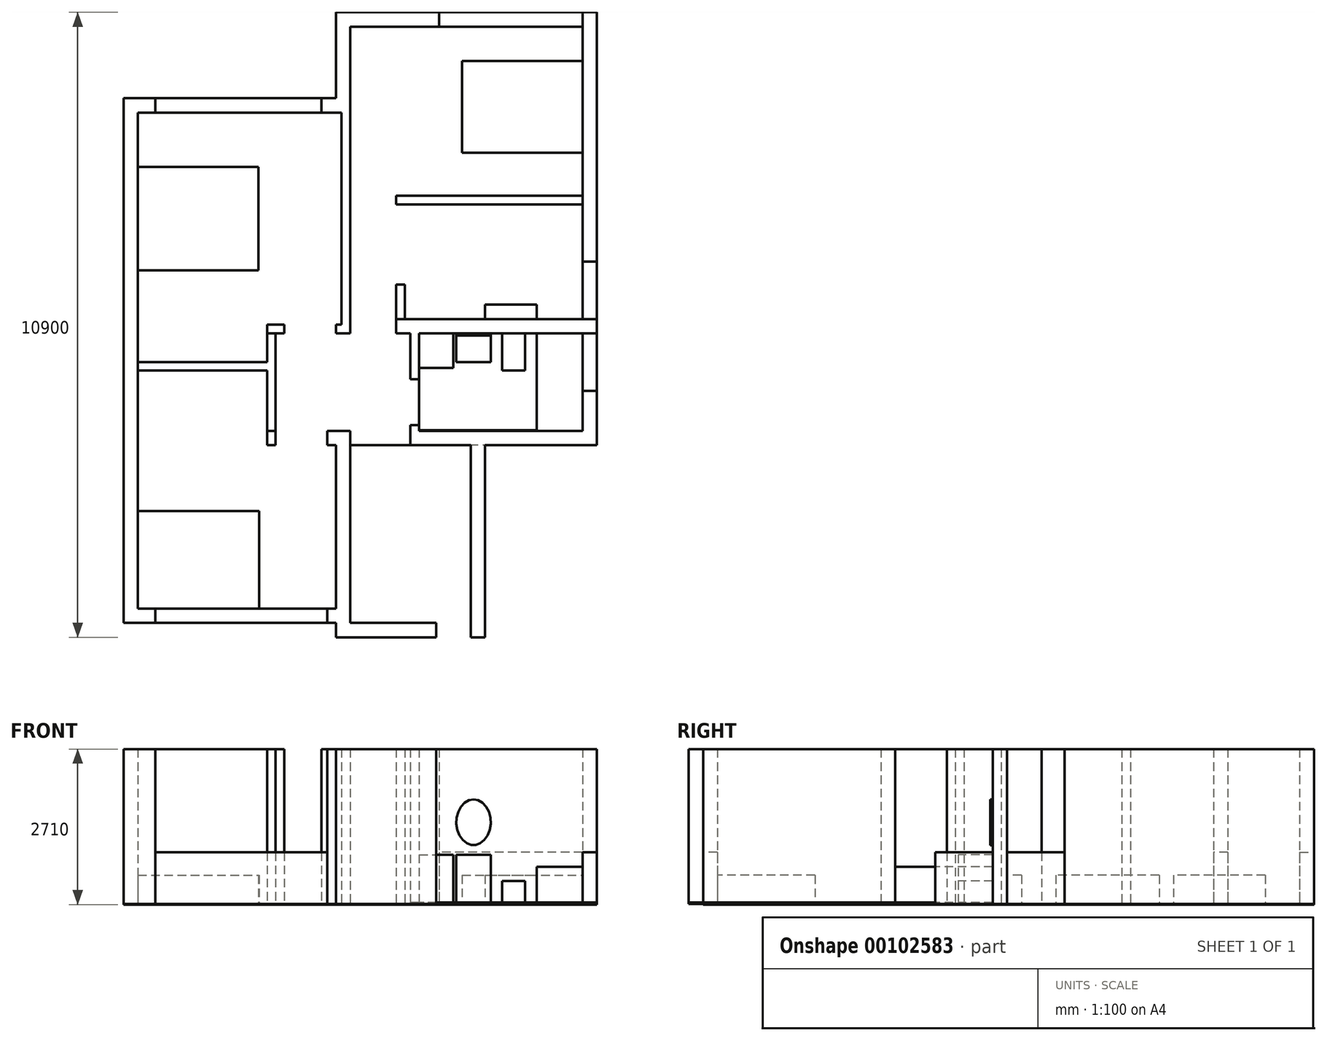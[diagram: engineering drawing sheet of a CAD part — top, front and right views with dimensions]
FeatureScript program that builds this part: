
annotation { "Feature Type Name" : "Feature", "Feature Type Description" : "" }
export const myFeature = defineFeature(function(context is Context, id is Id, definition is map)
    precondition{}
    {
        {
            var Q0;
            Q0=qCreatedBy(makeId("Top.planeOp"),FACE);
            var sketch = newSketch(context, id + "F0", { "sketchPlane" : qUnion([Q0])});
            skLineSegment(sketch, "E0.left", {"start": v(0, -3350) * mm, "end": v(0, 5800) * mm});
            skLineSegment(sketch, "E0.right", {"start": v(250, -250) * mm, "end": v(250, 5550) * mm});
            skLineSegment(sketch, "E1.bottom", {"start": v(0, 5800) * mm, "end": v(550, 5800) * mm});
            skLineSegment(sketch, "E1.top", {"start": v(250, 5550) * mm, "end": v(550, 5550) * mm});
            skLineSegment(sketch, "E1.right", {"start": v(550, 5800) * mm, "end": v(550, 5550) * mm});
            skLineSegment(sketch, "E2.top", {"start": v(0, -3350) * mm, "end": v(550, -3350) * mm});
            skLineSegment(sketch, "E2.right", {"start": v(250, -250) * mm, "end": v(250, -3100) * mm});
            skLineSegment(sketch, "E3.top", {"start": v(250, -3100) * mm, "end": v(550, -3100) * mm});
            skLineSegment(sketch, "E3.right", {"start": v(550, -3350) * mm, "end": v(550, -3100) * mm});
            skPoint(sketch, "E4.orphan", {"position": v(250, -3350) * mm});
            skLineSegment(sketch, "E5.bottom", {"start": v(3550, 0) * mm, "end": v(3950, 0) * mm});
            skLineSegment(sketch, "E5.top", {"start": v(3550, -250) * mm, "end": v(3700, -250) * mm});
            skLineSegment(sketch, "E5.left", {"start": v(3550, 0) * mm, "end": v(3550, -250) * mm});
            skLineSegment(sketch, "E5.right", {"start": v(3950, 0) * mm, "end": v(3950, -250) * mm});
            skLineSegment(sketch, "E6.bottom", {"start": v(3700, -3100) * mm, "end": v(3550, -3100) * mm});
            skLineSegment(sketch, "E6.top", {"start": v(3950, -3350) * mm, "end": v(3550, -3350) * mm});
            skLineSegment(sketch, "E6.left", {"start": v(3950, -3100) * mm, "end": v(3950, -3350) * mm});
            skLineSegment(sketch, "E6.right", {"start": v(3550, -3100) * mm, "end": v(3550, -3350) * mm});
            skLineSegment(sketch, "E7.left", {"start": v(3700, -250) * mm, "end": v(3700, -3100) * mm});
            skLineSegment(sketch, "E7.right", {"start": v(3950, -250) * mm, "end": v(3950, -3100) * mm});
            skLineSegment(sketch, "E8.bottom", {"start": v(3700, -3350) * mm, "end": v(5450, -3350) * mm});
            skLineSegment(sketch, "E8.top", {"start": v(3700, -3600) * mm, "end": v(5450, -3600) * mm});
            skLineSegment(sketch, "E8.left", {"start": v(3700, -3350) * mm, "end": v(3700, -3600) * mm});
            skLineSegment(sketch, "E8.right", {"start": v(5450, -3350) * mm, "end": v(5450, -3600) * mm});
            skLineSegment(sketch, "E9.top", {"start": v(6050, -3600) * mm, "end": v(6300, -3600) * mm});
            skLineSegment(sketch, "E9.left", {"start": v(6050, -250) * mm, "end": v(6050, -3600) * mm});
            skLineSegment(sketch, "E9.right", {"start": v(6300, -250) * mm, "end": v(6300, -3600) * mm});
            skLineSegment(sketch, "E10.bottom", {"start": v(5000, 0) * mm, "end": v(8125, 0) * mm});
            skLineSegment(sketch, "E10.top", {"start": v(5000, -250) * mm, "end": v(8125, -250) * mm});
            skLineSegment(sketch, "E10.left", {"start": v(5000, 0) * mm, "end": v(5000, -250) * mm});
            skPoint(sketch, "E11.endSnap0", {"position": v(3700, -1675) * mm});
            skLineSegment(sketch, "E12", {"start": v(3825, -963.9) * mm, "end": v(3825, 6299.29) * mm, "construction": true});
            skLineSegment(sketch, "E13", {"start": v(3550, -125) * mm, "end": v(6508.51, -125) * mm, "construction": true});
            skPoint(sketch, "E13.endSnap0", {"position": v(5250, -125) * mm});
            skLineSegment(sketch, "E14", {"start": v(8125, 470.93) * mm, "end": v(8125, -4199.5) * mm, "construction": true});
            skLineSegment(sketch, "E15", {"start": v(6175, -3600) * mm, "end": v(6175, 565.67) * mm, "construction": true});
            skPoint(sketch, "E15.endSnap0", {"position": v(6175, -3350) * mm});
            skPoint(sketch, "E16.orphan", {"position": v(5250, -250) * mm});
            skLineSegment(sketch, "E17", {"start": v(8125, 0) * mm, "end": v(8125, -250) * mm});
            skPoint(sketch, "E18.orphan", {"position": v(6050, -3350) * mm});
            skLineSegment(sketch, "E19.bottom", {"start": v(5000, 0) * mm, "end": v(5150, 0) * mm});
            skLineSegment(sketch, "E19.top", {"start": v(5000, 100) * mm, "end": v(5150, 100) * mm});
            skLineSegment(sketch, "E19.left", {"start": v(5000, 0) * mm, "end": v(5000, 100) * mm});
            skLineSegment(sketch, "E19.right", {"start": v(5150, 0) * mm, "end": v(5150, 100) * mm});
            skLineSegment(sketch, "E20.bottom", {"start": v(8125, 0) * mm, "end": v(8250, 0) * mm});
            skLineSegment(sketch, "E20.top", {"start": v(8125, -250) * mm, "end": v(8250, -250) * mm});
            skLineSegment(sketch, "E20.right", {"start": v(8250, 0) * mm, "end": v(8250, -250) * mm});
            skLineSegment(sketch, "E21.bottom", {"start": v(8250, 0) * mm, "end": v(8000, 0) * mm});
            skLineSegment(sketch, "E21.top", {"start": v(8250, 700) * mm, "end": v(8000, 700) * mm});
            skLineSegment(sketch, "E21.left", {"start": v(8250, 0) * mm, "end": v(8250, 700) * mm});
            skLineSegment(sketch, "E21.right", {"start": v(8000, 0) * mm, "end": v(8000, 700) * mm});
            skLineSegment(sketch, "E22.bottom", {"start": v(8250, 1700) * mm, "end": v(4750, 1700) * mm});
            skLineSegment(sketch, "E22.top", {"start": v(8250, 1950) * mm, "end": v(4750, 1950) * mm});
            skLineSegment(sketch, "E22.left", {"start": v(8250, 1700) * mm, "end": v(8250, 1950) * mm});
            skLineSegment(sketch, "E22.right", {"start": v(4750, 1700) * mm, "end": v(4750, 1950) * mm});
            skLineSegment(sketch, "E23.bottom", {"start": v(5000, 1700) * mm, "end": v(5150, 1700) * mm});
            skLineSegment(sketch, "E23.top", {"start": v(5000, 900) * mm, "end": v(5150, 900) * mm});
            skLineSegment(sketch, "E23.left", {"start": v(5000, 1700) * mm, "end": v(5000, 900) * mm});
            skLineSegment(sketch, "E23.right", {"start": v(5150, 1700) * mm, "end": v(5150, 900) * mm});
            skLineSegment(sketch, "E24.bottom", {"start": v(8250, 2950) * mm, "end": v(8000, 2950) * mm});
            skLineSegment(sketch, "E24.top", {"start": v(8250, 7300) * mm, "end": v(8000, 7300) * mm});
            skLineSegment(sketch, "E24.left", {"start": v(8250, 2950) * mm, "end": v(8250, 7300) * mm});
            skLineSegment(sketch, "E24.right", {"start": v(8000, 2950) * mm, "end": v(8000, 7300) * mm});
            skLineSegment(sketch, "E25", {"start": v(8250, 1825) * mm, "end": v(6731.2, 1825) * mm, "construction": true});
            skLineSegment(sketch, "E26", {"start": v(288.62, 5675) * mm, "end": v(10080.8, 5675) * mm, "construction": true});
            skPoint(sketch, "E27.firstSnap0", {"position": v(8125, 7300) * mm});
            skLineSegment(sketch, "E27.bottom", {"start": v(5500, 7300) * mm, "end": v(3950, 7300) * mm});
            skLineSegment(sketch, "E27.top", {"start": v(5500, 7050) * mm, "end": v(3950, 7050) * mm});
            skLineSegment(sketch, "E27.left", {"start": v(5500, 7300) * mm, "end": v(5500, 7050) * mm});
            skLineSegment(sketch, "E27.right", {"start": v(3950, 7300) * mm, "end": v(3950, 7050) * mm});
            skLineSegment(sketch, "E28.bottom", {"start": v(3950, 7300) * mm, "end": v(3700, 7300) * mm});
            skLineSegment(sketch, "E28.top", {"start": v(3950, 5550) * mm, "end": v(3700, 5550) * mm});
            skLineSegment(sketch, "E28.left", {"start": v(3950, 7300) * mm, "end": v(3950, 5550) * mm});
            skLineSegment(sketch, "E28.right", {"start": v(3700, 7300) * mm, "end": v(3700, 5550) * mm});
            skLineSegment(sketch, "E29.bottom", {"start": v(3700, 5550) * mm, "end": v(3450, 5550) * mm});
            skLineSegment(sketch, "E29.top", {"start": v(3700, 5800) * mm, "end": v(3450, 5800) * mm});
            skLineSegment(sketch, "E29.left", {"start": v(3700, 5550) * mm, "end": v(3700, 5800) * mm});
            skLineSegment(sketch, "E29.right", {"start": v(3450, 5550) * mm, "end": v(3450, 5800) * mm});
            skLineSegment(sketch, "E30.bottom", {"start": v(3800, 5550) * mm, "end": v(3950, 5550) * mm});
            skLineSegment(sketch, "E30.top", {"start": v(3800, 1700) * mm, "end": v(3950, 1700) * mm});
            skLineSegment(sketch, "E30.left", {"start": v(3800, 5550) * mm, "end": v(3800, 1700) * mm});
            skLineSegment(sketch, "E30.right", {"start": v(3950, 5550) * mm, "end": v(3950, 1700) * mm});
            skLineSegment(sketch, "E31.bottom", {"start": v(3800, 1700) * mm, "end": v(3700, 1700) * mm});
            skLineSegment(sketch, "E31.top", {"start": v(3800, 1850) * mm, "end": v(3700, 1850) * mm});
            skLineSegment(sketch, "E31.left", {"start": v(3800, 1700) * mm, "end": v(3800, 1850) * mm});
            skLineSegment(sketch, "E31.right", {"start": v(3700, 1700) * mm, "end": v(3700, 1850) * mm});
            skLineSegment(sketch, "E32.bottom", {"start": v(2800, 1700) * mm, "end": v(2500, 1700) * mm});
            skLineSegment(sketch, "E32.top", {"start": v(2800, 1850) * mm, "end": v(2500, 1850) * mm});
            skLineSegment(sketch, "E32.left", {"start": v(2800, 1700) * mm, "end": v(2800, 1850) * mm});
            skLineSegment(sketch, "E32.right", {"start": v(2500, 1700) * mm, "end": v(2500, 1850) * mm});
            skLineSegment(sketch, "E33.bottom", {"start": v(2650, -250) * mm, "end": v(2500, -250) * mm});
            skLineSegment(sketch, "E33.top", {"start": v(2650, 0) * mm, "end": v(2500, 0) * mm});
            skLineSegment(sketch, "E33.left", {"start": v(2650, -250) * mm, "end": v(2650, 0) * mm});
            skLineSegment(sketch, "E33.right", {"start": v(2500, -250) * mm, "end": v(2500, 0) * mm});
            skSolve(sketch);
        }
        {
            var Q0;
            Q0=qSketchRegion(id+"F0",true);
            extrude(context, id + "F1", {"entities" : qUnion([Q0]), "depth" : 2700 * mm});
        }
        {
            var Q0;
            Q0=qCreatedBy(makeId("Top.planeOp"),FACE);
            var sketch = newSketch(context, id + "F2", { "sketchPlane" : qUnion([Q0])});
            skLineSegment(sketch, "E34.bottom", {"start": v(8000, 7050) * mm, "end": v(5500, 7050) * mm});
            skLineSegment(sketch, "E34.top", {"start": v(8000, 7300) * mm, "end": v(5500, 7300) * mm});
            skLineSegment(sketch, "E34.left", {"start": v(8000, 7050) * mm, "end": v(8000, 7300) * mm});
            skLineSegment(sketch, "E34.right", {"start": v(5500, 7050) * mm, "end": v(5500, 7300) * mm});
            skLineSegment(sketch, "E35.bottom", {"start": v(8000, 2950) * mm, "end": v(8250, 2950) * mm});
            skLineSegment(sketch, "E35.top", {"start": v(8000, 1950) * mm, "end": v(8250, 1950) * mm});
            skLineSegment(sketch, "E35.left", {"start": v(8000, 2950) * mm, "end": v(8000, 1950) * mm});
            skLineSegment(sketch, "E35.right", {"start": v(8250, 2950) * mm, "end": v(8250, 1950) * mm});
            skLineSegment(sketch, "E36.bottom", {"start": v(550, -3100) * mm, "end": v(3550, -3100) * mm});
            skLineSegment(sketch, "E36.top", {"start": v(550, -3350) * mm, "end": v(3550, -3350) * mm});
            skLineSegment(sketch, "E36.left", {"start": v(550, -3100) * mm, "end": v(550, -3350) * mm});
            skLineSegment(sketch, "E36.right", {"start": v(3550, -3100) * mm, "end": v(3550, -3350) * mm});
            skLineSegment(sketch, "E37.bottom", {"start": v(550, 5800) * mm, "end": v(3450, 5800) * mm});
            skLineSegment(sketch, "E37.top", {"start": v(550, 5550) * mm, "end": v(3450, 5550) * mm});
            skLineSegment(sketch, "E37.left", {"start": v(550, 5800) * mm, "end": v(550, 5550) * mm});
            skLineSegment(sketch, "E37.right", {"start": v(3450, 5800) * mm, "end": v(3450, 5550) * mm});
            skLineSegment(sketch, "E38.bottom", {"start": v(8000, 1700) * mm, "end": v(8250, 1700) * mm});
            skLineSegment(sketch, "E38.top", {"start": v(8000, 700) * mm, "end": v(8250, 700) * mm});
            skLineSegment(sketch, "E38.left", {"start": v(8000, 1700) * mm, "end": v(8000, 700) * mm});
            skLineSegment(sketch, "E38.right", {"start": v(8250, 1700) * mm, "end": v(8250, 700) * mm});
            skSolve(sketch);
        }
        {
            var Q0;
            Q0=makeQuery(id+"F2.imprint","IMPRINT",FACE,{"disambiguationData":[TD([[makeQuery(id+"F2.imprint","IMPRINT",EDGE,{"derivedFrom":sQuery(id+"F2.wireOp",EDGE,"E34.bottom")}),-1.0]])]});
            var Q1;
            Q1=makeQuery(id+"F2.imprint","IMPRINT",FACE,{"disambiguationData":[TD([[makeQuery(id+"F2.imprint","IMPRINT",EDGE,{"derivedFrom":sQuery(id+"F2.wireOp",EDGE,"E37.bottom")}),-1.0]])]});
            var Q2;
            Q2=makeQuery(id+"F2.imprint","IMPRINT",FACE,{"disambiguationData":[TD([[makeQuery(id+"F2.imprint","IMPRINT",EDGE,{"derivedFrom":sQuery(id+"F2.wireOp",EDGE,"E36.bottom")}),-1.0]])]});
            var Q3;
            Q3=makeQuery(id+"F2.imprint","IMPRINT",FACE,{"disambiguationData":[TD([[makeQuery(id+"F2.imprint","IMPRINT",EDGE,{"derivedFrom":sQuery(id+"F2.wireOp",EDGE,"E35.bottom")}),-1.0]])]});
            var Q4;
            Q4=makeQuery(id+"F2.imprint","IMPRINT",FACE,{"disambiguationData":[TD([[makeQuery(id+"F2.imprint","IMPRINT",EDGE,{"derivedFrom":sQuery(id+"F2.wireOp",EDGE,"E38.bottom")}),-1.0]])]});
            extrude(context, id + "F3", {"entities" : qUnion([Q0, Q1, Q2, Q3, Q4]), "depth" : 900 * mm});
        }
        {
            var Q0;
            Q0=qCreatedBy(makeId("Top.planeOp"),FACE);
            var sketch = newSketch(context, id + "F4", { "sketchPlane" : qUnion([Q0])});
            skLineSegment(sketch, "E39", {"start": v(0, -3241.89) * mm, "end": v(0, 5800) * mm});
            skLineSegment(sketch, "E40", {"start": v(0, 5800) * mm, "end": v(3700, 5800) * mm});
            skLineSegment(sketch, "E41", {"start": v(3700, 5800) * mm, "end": v(3700, 7300) * mm});
            skLineSegment(sketch, "E42", {"start": v(3700, 7300) * mm, "end": v(8250, 7300) * mm});
            skLineSegment(sketch, "E43", {"start": v(8250, 7300) * mm, "end": v(8250, -250) * mm});
            skLineSegment(sketch, "E44", {"start": v(8250, -250) * mm, "end": v(3950, -250) * mm});
            skLineSegment(sketch, "E45", {"start": v(3950, -250) * mm, "end": v(3950, -3350) * mm});
            skLineSegment(sketch, "E46", {"start": v(3950, -3350) * mm, "end": v(0, -3350) * mm});
            skLineSegment(sketch, "E47", {"start": v(0, -3350) * mm, "end": v(0, -3241.89) * mm});
            skSolve(sketch);
        }
        {
            var Q0;
            Q0=qSketchRegion(id+"F4",true);
            extrude(context, id + "F5", {"entities" : qUnion([Q0]), "oppositeDirection" : true, "depth" : 10 * mm});
        }
        {
            var Q0;
            Q0=makeQuery(id+"F5.opExtrude","CAP_FACE",FACE,{"disambiguationData":[OSD([sQuery(id+"F4.wireOp",EDGE,"E39"),sQuery(id+"F4.wireOp",EDGE,"E40"),sQuery(id+"F4.wireOp",EDGE,"E41"),sQuery(id+"F4.wireOp",EDGE,"E42"),sQuery(id+"F4.wireOp",EDGE,"E43"),sQuery(id+"F4.wireOp",EDGE,"E44"),sQuery(id+"F4.wireOp",EDGE,"E45"),sQuery(id+"F4.wireOp",EDGE,"E46"),sQuery(id+"F4.wireOp",EDGE,"E47")])],"isStart":true});
            var sketch = newSketch(context, id + "F6", { "sketchPlane" : qUnion([Q0])});
            skLineSegment(sketch, "E48.bottom", {"start": v(6300, 2200) * mm, "end": v(7200, 2200) * mm});
            skLineSegment(sketch, "E48.top", {"start": v(6300, 1950) * mm, "end": v(7200, 1950) * mm});
            skLineSegment(sketch, "E48.left", {"start": v(6300, 2200) * mm, "end": v(6300, 1950) * mm});
            skLineSegment(sketch, "E48.right", {"start": v(7200, 2200) * mm, "end": v(7200, 1950) * mm});
            skSolve(sketch);
        }
        {
            var Q0;
            Q0=makeQuery(id+"F6.imprint","IMPRINT",FACE,{"disambiguationData":[TD([[makeQuery(id+"F6.imprint","IMPRINT",EDGE,{"derivedFrom":sQuery(id+"F6.wireOp",EDGE,"E48.bottom")}),-1.0]])]});
            extrude(context, id + "F7", {"entities" : qUnion([Q0]), "depth" : 500 * mm});
        }
        {
            var Q0;
            Q0=makeQuery(id+"F5.opExtrude","CAP_FACE",FACE,{"disambiguationData":[OSD([sQuery(id+"F4.wireOp",EDGE,"E39"),sQuery(id+"F4.wireOp",EDGE,"E40"),sQuery(id+"F4.wireOp",EDGE,"E41"),sQuery(id+"F4.wireOp",EDGE,"E42"),sQuery(id+"F4.wireOp",EDGE,"E43"),sQuery(id+"F4.wireOp",EDGE,"E44"),sQuery(id+"F4.wireOp",EDGE,"E45"),sQuery(id+"F4.wireOp",EDGE,"E46"),sQuery(id+"F4.wireOp",EDGE,"E47")])],"isStart":true});
            var sketch = newSketch(context, id + "F8", { "sketchPlane" : qUnion([Q0])});
            skLineSegment(sketch, "E49.bottom", {"start": v(4750, 4100) * mm, "end": v(8000, 4100) * mm});
            skLineSegment(sketch, "E49.top", {"start": v(4750, 3950) * mm, "end": v(8000, 3950) * mm});
            skLineSegment(sketch, "E49.left", {"start": v(4750, 3950) * mm, "end": v(4750, 3450) * mm});
            skLineSegment(sketch, "E49.right", {"start": v(8000, 4100) * mm, "end": v(8000, 3950) * mm});
            skLineSegment(sketch, "E50.bottom", {"start": v(4750, 3950) * mm, "end": v(4900, 3950) * mm});
            skLineSegment(sketch, "E50.top", {"start": v(4750, 3350) * mm, "end": v(4900, 3350) * mm});
            skLineSegment(sketch, "E50.left", {"start": v(4750, 3450) * mm, "end": v(4750, 3350) * mm});
            skLineSegment(sketch, "E50.right", {"start": v(4900, 3950) * mm, "end": v(4900, 3350) * mm});
            skLineSegment(sketch, "E51.bottom", {"start": v(4750, 2550) * mm, "end": v(4900, 2550) * mm});
            skLineSegment(sketch, "E51.top", {"start": v(4750, 1950) * mm, "end": v(4900, 1950) * mm});
            skLineSegment(sketch, "E51.left", {"start": v(4750, 2550) * mm, "end": v(4750, 1950) * mm});
            skLineSegment(sketch, "E51.right", {"start": v(4900, 2550) * mm, "end": v(4900, 1950) * mm});
            skLineSegment(sketch, "E52", {"start": v(4750, 4100) * mm, "end": v(4750, 3950) * mm});
            skSolve(sketch);
        }
        {
            var Q0;
            Q0=makeQuery(id+"F8.imprint","IMPRINT",FACE,{"disambiguationData":[TD([[makeQuery(id+"F8.imprint","IMPRINT",EDGE,{"derivedFrom":sQuery(id+"F8.wireOp",EDGE,"E49.bottom")}),-1.0]])]});
            var Q1;
            Q1=makeQuery(id+"F8.imprint","IMPRINT",FACE,{"disambiguationData":[TD([[makeQuery(id+"F8.imprint","IMPRINT",EDGE,{"derivedFrom":sQuery(id+"F8.wireOp",EDGE,"E50.bottom")}),-1.0]])]});
            var Q2;
            Q2=makeQuery(id+"F8.imprint","IMPRINT",FACE,{"disambiguationData":[TD([[makeQuery(id+"F8.imprint","IMPRINT",EDGE,{"derivedFrom":sQuery(id+"F8.wireOp",EDGE,"E51.bottom")}),-1.0]])]});
            extrude(context, id + "F9", {"entities" : qUnion([Q0, Q1, Q2]), "depth" : 2700 * mm});
        }
        {
            var Q0;
            Q0=makeQuery(id+"F5.opExtrude","CAP_FACE",FACE,{"disambiguationData":[OSD([sQuery(id+"F4.wireOp",EDGE,"E39"),sQuery(id+"F4.wireOp",EDGE,"E40"),sQuery(id+"F4.wireOp",EDGE,"E41"),sQuery(id+"F4.wireOp",EDGE,"E42"),sQuery(id+"F4.wireOp",EDGE,"E43"),sQuery(id+"F4.wireOp",EDGE,"E44"),sQuery(id+"F4.wireOp",EDGE,"E45"),sQuery(id+"F4.wireOp",EDGE,"E46"),sQuery(id+"F4.wireOp",EDGE,"E47")])],"isStart":true});
            var sketch = newSketch(context, id + "F10", { "sketchPlane" : qUnion([Q0])});
            skLineSegment(sketch, "E53.bottom", {"start": v(2500, 0) * mm, "end": v(2650, 0) * mm});
            skLineSegment(sketch, "E53.top", {"start": v(2500, 1700) * mm, "end": v(2650, 1700) * mm});
            skLineSegment(sketch, "E53.left", {"start": v(2500, 0) * mm, "end": v(2500, 1700) * mm});
            skLineSegment(sketch, "E53.right", {"start": v(2650, 0) * mm, "end": v(2650, 1700) * mm});
            skLineSegment(sketch, "E54.bottom", {"start": v(250, 1200) * mm, "end": v(2500, 1200) * mm});
            skLineSegment(sketch, "E54.top", {"start": v(250, 1050) * mm, "end": v(2500, 1050) * mm});
            skLineSegment(sketch, "E54.left", {"start": v(250, 1200) * mm, "end": v(250, 1050) * mm});
            skLineSegment(sketch, "E54.right", {"start": v(2500, 1200) * mm, "end": v(2500, 1050) * mm});
            skSolve(sketch);
        }
        {
            var Q0;
            Q0 = qSketchRegion(id + "F10", true);
            extrude(context, id + "F11", {"entities" : qUnion([Q0]), "depth" : 2700 * mm});
        }
        {
            var Q0;
            Q0=makeQuery(id+"F5.opExtrude","CAP_FACE",FACE,{"disambiguationData":[OSD([sQuery(id+"F4.wireOp",EDGE,"E39"),sQuery(id+"F4.wireOp",EDGE,"E40"),sQuery(id+"F4.wireOp",EDGE,"E41"),sQuery(id+"F4.wireOp",EDGE,"E42"),sQuery(id+"F4.wireOp",EDGE,"E43"),sQuery(id+"F4.wireOp",EDGE,"E44"),sQuery(id+"F4.wireOp",EDGE,"E45"),sQuery(id+"F4.wireOp",EDGE,"E46"),sQuery(id+"F4.wireOp",EDGE,"E47")])],"isStart":true});
            var sketch = newSketch(context, id + "F12", { "sketchPlane" : qUnion([Q0])});
            skLineSegment(sketch, "E55.bottom", {"start": v(250, -250) * mm, "end": v(2500, -250) * mm});
            skLineSegment(sketch, "E55.top", {"start": v(250, -100) * mm, "end": v(2500, -100) * mm});
            skLineSegment(sketch, "E55.left", {"start": v(250, -250) * mm, "end": v(250, -100) * mm});
            skLineSegment(sketch, "E55.right", {"start": v(2500, -250) * mm, "end": v(2500, -100) * mm});
            skLineSegment(sketch, "E56.bottom", {"start": v(250, 1850) * mm, "end": v(2500, 1850) * mm});
            skLineSegment(sketch, "E56.top", {"start": v(250, 1700) * mm, "end": v(2500, 1700) * mm});
            skLineSegment(sketch, "E56.left", {"start": v(250, 1850) * mm, "end": v(250, 1700) * mm});
            skLineSegment(sketch, "E56.right", {"start": v(2500, 1850) * mm, "end": v(2500, 1700) * mm});
            skLineSegment(sketch, "E57.bottom", {"start": v(2500, 925.22) * mm, "end": v(2540, 925.22) * mm});
            skLineSegment(sketch, "E57.top", {"start": v(2500, 0) * mm, "end": v(2540, 0) * mm});
            skLineSegment(sketch, "E57.left", {"start": v(2500, 925.22) * mm, "end": v(2500, 0) * mm});
            skLineSegment(sketch, "E57.right", {"start": v(2540, 925.22) * mm, "end": v(2540, 0) * mm});
            skLineSegment(sketch, "E58.bottom", {"start": v(2540, 925.22) * mm, "end": v(2580, 925.22) * mm});
            skLineSegment(sketch, "E58.top", {"start": v(2540, 1700) * mm, "end": v(2580, 1700) * mm});
            skLineSegment(sketch, "E58.left", {"start": v(2540, 925.22) * mm, "end": v(2540, 1700) * mm});
            skLineSegment(sketch, "E58.right", {"start": v(2580, 925.22) * mm, "end": v(2580, 1700) * mm});
            skSolve(sketch);
        }
        {
            var Q0;
            Q0=makeQuery(id+"F5.opExtrude","CAP_FACE",FACE,{"disambiguationData":[OSD([sQuery(id+"F4.wireOp",EDGE,"E39"),sQuery(id+"F4.wireOp",EDGE,"E40"),sQuery(id+"F4.wireOp",EDGE,"E41"),sQuery(id+"F4.wireOp",EDGE,"E42"),sQuery(id+"F4.wireOp",EDGE,"E43"),sQuery(id+"F4.wireOp",EDGE,"E44"),sQuery(id+"F4.wireOp",EDGE,"E45"),sQuery(id+"F4.wireOp",EDGE,"E46"),sQuery(id+"F4.wireOp",EDGE,"E47")])],"isStart":true});
            var sketch = newSketch(context, id + "F13", { "sketchPlane" : qUnion([Q0])});
            skLineSegment(sketch, "E59.bottom", {"start": v(5900, 6450) * mm, "end": v(8000, 6450) * mm});
            skLineSegment(sketch, "E59.top", {"start": v(5900, 4850) * mm, "end": v(8000, 4850) * mm});
            skLineSegment(sketch, "E59.left", {"start": v(5900, 6450) * mm, "end": v(5900, 4850) * mm});
            skLineSegment(sketch, "E59.right", {"start": v(8000, 6450) * mm, "end": v(8000, 4850) * mm});
            skLineSegment(sketch, "E60.bottom", {"start": v(250, 4600) * mm, "end": v(2350, 4600) * mm});
            skLineSegment(sketch, "E60.top", {"start": v(250, 2800) * mm, "end": v(2350, 2800) * mm});
            skLineSegment(sketch, "E60.left", {"start": v(250, 4600) * mm, "end": v(250, 2800) * mm});
            skLineSegment(sketch, "E60.right", {"start": v(2350, 4600) * mm, "end": v(2350, 2800) * mm});
            skLineSegment(sketch, "E61.bottom", {"start": v(250, -1400) * mm, "end": v(2360, -1400) * mm});
            skLineSegment(sketch, "E61.top", {"start": v(250, -3100) * mm, "end": v(2360, -3100) * mm});
            skLineSegment(sketch, "E61.left", {"start": v(250, -1400) * mm, "end": v(250, -3100) * mm});
            skLineSegment(sketch, "E61.right", {"start": v(2360, -1400) * mm, "end": v(2360, -3100) * mm});
            skLineSegment(sketch, "E62", {"start": v(250, -2200) * mm, "end": v(2360, -2200) * mm});
            skSolve(sketch);
        }
        {
            var Q0;
            Q0 = qSketchRegion(id + "F13", true);
            extrude(context, id + "F14", {"entities" : qUnion([Q0]), "depth" : 500 * mm});
        }
        {
            var Q0;
            Q0=makeQuery(id+"F5.opExtrude","CAP_FACE",FACE,{"disambiguationData":[OSD([sQuery(id+"F4.wireOp",EDGE,"E39"),sQuery(id+"F4.wireOp",EDGE,"E40"),sQuery(id+"F4.wireOp",EDGE,"E41"),sQuery(id+"F4.wireOp",EDGE,"E42"),sQuery(id+"F4.wireOp",EDGE,"E43"),sQuery(id+"F4.wireOp",EDGE,"E44"),sQuery(id+"F4.wireOp",EDGE,"E45"),sQuery(id+"F4.wireOp",EDGE,"E46"),sQuery(id+"F4.wireOp",EDGE,"E47")])],"isStart":true});
            var sketch = newSketch(context, id + "F15", { "sketchPlane" : qUnion([Q0])});
            skLineSegment(sketch, "E63.bottom", {"start": v(7200, 1700) * mm, "end": v(8000, 1700) * mm});
            skLineSegment(sketch, "E63.top", {"start": v(7200, 0) * mm, "end": v(8000, 0) * mm});
            skLineSegment(sketch, "E63.left", {"start": v(7200, 1700) * mm, "end": v(7200, 0) * mm});
            skLineSegment(sketch, "E63.right", {"start": v(8000, 1700) * mm, "end": v(8000, 0) * mm});
            skSolve(sketch);
        }
        {
            var Q0;
            Q0=makeQuery(id+"F15.imprint","IMPRINT",FACE,{"disambiguationData":[TD([[makeQuery(id+"F15.imprint","IMPRINT",EDGE,{"derivedFrom":sQuery(id+"F15.wireOp",EDGE,"E63.bottom")}),-1.0]])]});
            extrude(context, id + "F16", {"entities" : qUnion([Q0]), "depth" : 650 * mm});
        }
        {
            var Q0;
            Q0=makeQuery(id+"F5.opExtrude","CAP_FACE",FACE,{"disambiguationData":[OSD([sQuery(id+"F4.wireOp",EDGE,"E39"),sQuery(id+"F4.wireOp",EDGE,"E40"),sQuery(id+"F4.wireOp",EDGE,"E41"),sQuery(id+"F4.wireOp",EDGE,"E42"),sQuery(id+"F4.wireOp",EDGE,"E43"),sQuery(id+"F4.wireOp",EDGE,"E44"),sQuery(id+"F4.wireOp",EDGE,"E45"),sQuery(id+"F4.wireOp",EDGE,"E46"),sQuery(id+"F4.wireOp",EDGE,"E47")])],"isStart":true});
            var sketch = newSketch(context, id + "F17", { "sketchPlane" : qUnion([Q0])});
            skLineSegment(sketch, "E64.bottom", {"start": v(5150, 1700) * mm, "end": v(5750, 1700) * mm});
            skLineSegment(sketch, "E64.top", {"start": v(5150, 1100) * mm, "end": v(5750, 1100) * mm});
            skLineSegment(sketch, "E64.left", {"start": v(5150, 1700) * mm, "end": v(5150, 1100) * mm});
            skLineSegment(sketch, "E64.right", {"start": v(5750, 1700) * mm, "end": v(5750, 1100) * mm});
            skSolve(sketch);
        }
        {
            var Q0;
            Q0 = qSketchRegion(id + "F17", true);
            extrude(context, id + "F18", {"entities" : qUnion([Q0]), "depth" : 860 * mm});
        }
        {
            var Q0;
            Q0=makeQuery(id+"F5.opExtrude","CAP_FACE",FACE,{"disambiguationData":[OSD([sQuery(id+"F4.wireOp",EDGE,"E39"),sQuery(id+"F4.wireOp",EDGE,"E40"),sQuery(id+"F4.wireOp",EDGE,"E41"),sQuery(id+"F4.wireOp",EDGE,"E42"),sQuery(id+"F4.wireOp",EDGE,"E43"),sQuery(id+"F4.wireOp",EDGE,"E44"),sQuery(id+"F4.wireOp",EDGE,"E45"),sQuery(id+"F4.wireOp",EDGE,"E46"),sQuery(id+"F4.wireOp",EDGE,"E47")])],"isStart":true});
            var sketch = newSketch(context, id + "F19", { "sketchPlane" : qUnion([Q0])});
            skLineSegment(sketch, "E65.bottom", {"start": v(5800, 1700) * mm, "end": v(6400, 1700) * mm});
            skLineSegment(sketch, "E65.top", {"start": v(5800, 1200) * mm, "end": v(6400, 1200) * mm});
            skLineSegment(sketch, "E65.left", {"start": v(5800, 1700) * mm, "end": v(5800, 1200) * mm});
            skLineSegment(sketch, "E65.right", {"start": v(6400, 1700) * mm, "end": v(6400, 1200) * mm});
            skLineSegment(sketch, "E66", {"start": v(6100, 1700) * mm, "end": v(6100, 1402.26) * mm, "construction": true});
            skSolve(sketch);
        }
        {
            var Q0;
            Q0 = qSketchRegion(id + "F19", true);
            extrude(context, id + "F20", {"entities" : qUnion([Q0]), "depth" : 860 * mm});
        }
        {
            var Q0;
            Q0=makeQuery(id+"F5.opExtrude","CAP_FACE",FACE,{"disambiguationData":[OSD([sQuery(id+"F4.wireOp",EDGE,"E39"),sQuery(id+"F4.wireOp",EDGE,"E40"),sQuery(id+"F4.wireOp",EDGE,"E41"),sQuery(id+"F4.wireOp",EDGE,"E42"),sQuery(id+"F4.wireOp",EDGE,"E43"),sQuery(id+"F4.wireOp",EDGE,"E44"),sQuery(id+"F4.wireOp",EDGE,"E45"),sQuery(id+"F4.wireOp",EDGE,"E46"),sQuery(id+"F4.wireOp",EDGE,"E47")])],"isStart":true});
            var sketch = newSketch(context, id + "F21", { "sketchPlane" : qUnion([Q0])});
            skLineSegment(sketch, "E67.bottom", {"start": v(6600, 1700) * mm, "end": v(7000, 1700) * mm});
            skLineSegment(sketch, "E67.top", {"start": v(6600, 1050) * mm, "end": v(7000, 1050) * mm});
            skLineSegment(sketch, "E67.left", {"start": v(6600, 1700) * mm, "end": v(6600, 1050) * mm});
            skLineSegment(sketch, "E67.right", {"start": v(7000, 1700) * mm, "end": v(7000, 1050) * mm});
            skLineSegment(sketch, "E68", {"start": v(6800, 1700) * mm, "end": v(6800, 1387.73) * mm, "construction": true});
            skSolve(sketch);
        }
        {
            var Q0;
            Q0 = qSketchRegion(id + "F21", true);
            extrude(context, id + "F22", {"entities" : qUnion([Q0]), "depth" : 400 * mm});
        }
        {
            var Q0;
            Q0=makeQuery(id+"F5.opExtrude","CAP_FACE",FACE,{"disambiguationData":[OSD([sQuery(id+"F4.wireOp",EDGE,"E39"),sQuery(id+"F4.wireOp",EDGE,"E40"),sQuery(id+"F4.wireOp",EDGE,"E41"),sQuery(id+"F4.wireOp",EDGE,"E42"),sQuery(id+"F4.wireOp",EDGE,"E43"),sQuery(id+"F4.wireOp",EDGE,"E44"),sQuery(id+"F4.wireOp",EDGE,"E45"),sQuery(id+"F4.wireOp",EDGE,"E46"),sQuery(id+"F4.wireOp",EDGE,"E47")])],"isStart":true});
            var sketch = newSketch(context, id + "F23", { "sketchPlane" : qUnion([Q0])});
            skLineSegment(sketch, "E69.bottom", {"start": v(5150, 1700) * mm, "end": v(8000, 1700) * mm});
            skLineSegment(sketch, "E69.top", {"start": v(5150, 10) * mm, "end": v(8000, 10) * mm});
            skLineSegment(sketch, "E69.left", {"start": v(5150, 1700) * mm, "end": v(5150, 10) * mm});
            skLineSegment(sketch, "E69.right", {"start": v(8000, 1700) * mm, "end": v(8000, 10) * mm});
            skSolve(sketch);
        }
        {
            var Q0;
            Q0=makeQuery(id+"F23.imprint","IMPRINT",FACE,{"disambiguationData":[TD([[makeQuery(id+"F23.imprint","IMPRINT",EDGE,{"derivedFrom":sQuery(id+"F23.wireOp",EDGE,"E69.bottom")}),-1.0]])]});
            extrude(context, id + "F24", {"entities" : qUnion([Q0]), "depth" : 25 * mm});
        }
        {
            var Q0;
            {var subQ0=sQuery(id+"F0.wireOp",EDGE,"E22.bottom");Q0=makeQuery(id+"F1.opExtrude","SWEPT_FACE",FACE,{"disambiguationData":[OSD([subQ0]),TDD([makeQuery(id+"F0.imprint","IMPRINT",EDGE,{"disambiguationData":[TD([[makeQuery(id+"F0.imprint","INTERSECT",VERTEX,{"derivedFrom":[subQ0,sQuery(id+"F0.wireOp",EDGE,"E22.left")]}),-1.0]])],"derivedFrom":subQ0})])]});}
            var sketch = newSketch(context, id + "F25", { "sketchPlane" : qUnion([Q0])});
            skLineSegment(sketch, "E70.bottom", {"start": v(5150, 2100) * mm, "end": v(8250, 2100) * mm});
            skLineSegment(sketch, "E70.top", {"start": v(5150, 0) * mm, "end": v(8250, 0) * mm});
            skLineSegment(sketch, "E70.left", {"start": v(5150, 2100) * mm, "end": v(5150, 0) * mm});
            skLineSegment(sketch, "E70.right", {"start": v(8250, 2100) * mm, "end": v(8250, 0) * mm});
            skSolve(sketch);
        }
        {
            var Q0;
            Q0=makeQuery(id+"F1.opExtrude","CAP_FACE",FACE,{"disambiguationData":[OSD([sQuery(id+"F0.wireOp",EDGE,"E9.top"),sQuery(id+"F0.wireOp",EDGE,"E9.left"),sQuery(id+"F0.wireOp",EDGE,"E9.right"),sQuery(id+"F0.wireOp",EDGE,"E10.bottom"),sQuery(id+"F0.wireOp",EDGE,"E10.top"),sQuery(id+"F0.wireOp",EDGE,"E10.left"),sQuery(id+"F0.wireOp",EDGE,"E19.top"),sQuery(id+"F0.wireOp",EDGE,"E19.left"),sQuery(id+"F0.wireOp",EDGE,"E19.right"),sQuery(id+"F0.wireOp",EDGE,"E20.top"),sQuery(id+"F0.wireOp",EDGE,"E20.right"),sQuery(id+"F0.wireOp",EDGE,"E21.top"),sQuery(id+"F0.wireOp",EDGE,"E21.left"),sQuery(id+"F0.wireOp",EDGE,"E21.right")])],"isStart":false});
            var Q1;
            Q1=makeQuery(id+"F24.opExtrude","CAP_FACE",FACE,{"disambiguationData":[OSD([sQuery(id+"F23.wireOp",EDGE,"E69.bottom"),sQuery(id+"F23.wireOp",EDGE,"E69.top"),sQuery(id+"F23.wireOp",EDGE,"E69.left"),sQuery(id+"F23.wireOp",EDGE,"E69.right")])],"isStart":false});
            extrude(context, id + "F26", {"entities" : qUnion([Q0]), "operationType" : NewBodyOperationType.REMOVE, "endBound" : BoundingType.UP_TO_SURFACE, "oppositeDirection" : true, "depth" : 25 * mm, "endBoundEntityFace" : qUnion([Q1]), "offsetDistance" : 25 * mm});
        }
        {
            var Q0;
            Q0=makeQuery(id+"F25.imprint","IMPRINT",FACE,{"disambiguationData":[TD([[makeQuery(id+"F25.imprint","IMPRINT",EDGE,{"derivedFrom":sQuery(id+"F25.wireOp",EDGE,"E70.bottom")}),-1.0]])]});
            var sketch = newSketch(context, id + "F27", { "sketchPlane" : qUnion([Q0])});
            skPoint(sketch, "E71.middle", {"position": v(6100, 1425) * mm});
            skEllipse(sketch, "E72", {"center": v(6100, 1425) * mm, "majorRadius": 400 * mm, "minorRadius": 300 * mm, "majorAxis": v(0, 1)});
            skFitSpline(sketch, "E73.0", {"points": [v(6106.8, 1804.92) * mm, v(6100, 1805.04) * mm, v(6093.2, 1804.92) * mm, v(6084.19, 1804.48) * mm, v(6072.96, 1803.36) * mm, v(6059.59, 1801.15) * mm, v(6041.91, 1797.03) * mm, v(6020.15, 1789.74) * mm, v(5994.72, 1777.6) * mm, v(5974.25, 1764.7) * mm, v(5958.4, 1752.75) * mm, v(5946.8, 1742.98) * mm, v(5935.5, 1732.4) * mm, v(5926.39, 1722.93) * mm, v(5919.27, 1714.97) * mm, v(5914.03, 1708.8) * mm, v(5909.75, 1703.5) * mm, v(5906.37, 1699.15) * mm, v(5903.86, 1695.85) * mm, v(5901.38, 1692.5) * mm, v(5898.13, 1688) * mm, v(5894.13, 1682.26) * mm, v(5889.48, 1675.23) * mm, v(5883.45, 1665.66) * mm, v(5876.26, 1653.36) * mm, v(5868.2, 1638.06) * mm, v(5860.7, 1622.26) * mm, v(5851.51, 1600.57) * mm, v(5841.52, 1572.38) * mm, v(5833.62, 1542.97) * mm, v(5828.6, 1518.84) * mm, v(5825.48, 1500.47) * mm, v(5823.05, 1481.87) * mm, v(5821.59, 1466.2) * mm, v(5820.77, 1453.6) * mm, v(5820.33, 1444.1) * mm, v(5820.1, 1436.15) * mm, v(5820.01, 1429.78) * mm, v(5820, 1425) * mm, v(5820.01, 1420.22) * mm, v(5820.1, 1413.85) * mm, v(5820.33, 1405.9) * mm, v(5820.77, 1396.4) * mm, v(5821.59, 1383.8) * mm, v(5823.05, 1368.13) * mm, v(5825.48, 1349.53) * mm, v(5828.6, 1331.16) * mm, v(5833.62, 1307.03) * mm, v(5841.52, 1277.62) * mm, v(5851.51, 1249.43) * mm, v(5860.7, 1227.74) * mm, v(5868.2, 1211.94) * mm, v(5876.26, 1196.64) * mm, v(5883.45, 1184.34) * mm, v(5889.48, 1174.77) * mm, v(5894.13, 1167.74) * mm, v(5898.13, 1162) * mm, v(5901.38, 1157.5) * mm, v(5903.86, 1154.15) * mm, v(5906.37, 1150.85) * mm, v(5909.75, 1146.5) * mm, v(5914.03, 1141.2) * mm, v(5919.27, 1135.03) * mm, v(5926.39, 1127.07) * mm, v(5935.5, 1117.6) * mm, v(5946.8, 1107.02) * mm, v(5958.4, 1097.25) * mm, v(5974.25, 1085.3) * mm, v(5994.72, 1072.4) * mm, v(6020.15, 1060.26) * mm, v(6041.91, 1052.97) * mm, v(6059.59, 1048.85) * mm, v(6072.96, 1046.64) * mm, v(6084.19, 1045.52) * mm, v(6093.2, 1045.08) * mm, v(6100, 1044.96) * mm, v(6106.8, 1045.08) * mm, v(6115.81, 1045.52) * mm, v(6127.04, 1046.64) * mm, v(6140.41, 1048.85) * mm, v(6158.09, 1052.97) * mm, v(6179.85, 1060.26) * mm, v(6205.28, 1072.4) * mm, v(6225.75, 1085.3) * mm, v(6241.6, 1097.25) * mm, v(6253.2, 1107.02) * mm, v(6264.5, 1117.6) * mm, v(6273.61, 1127.07) * mm, v(6280.73, 1135.03) * mm, v(6285.97, 1141.2) * mm, v(6290.25, 1146.5) * mm, v(6293.63, 1150.85) * mm, v(6296.14, 1154.15) * mm, v(6298.62, 1157.5) * mm, v(6301.87, 1162) * mm, v(6305.87, 1167.74) * mm, v(6310.52, 1174.77) * mm, v(6316.55, 1184.34) * mm, v(6323.74, 1196.64) * mm, v(6331.8, 1211.94) * mm, v(6339.3, 1227.74) * mm, v(6348.49, 1249.43) * mm, v(6358.48, 1277.62) * mm, v(6366.38, 1307.03) * mm, v(6371.4, 1331.16) * mm, v(6374.52, 1349.53) * mm, v(6376.95, 1368.13) * mm, v(6378.41, 1383.8) * mm, v(6379.23, 1396.4) * mm, v(6379.67, 1405.9) * mm, v(6379.9, 1413.85) * mm, v(6379.99, 1420.22) * mm, v(6380, 1425) * mm, v(6379.99, 1429.78) * mm, v(6379.9, 1436.15) * mm, v(6379.67, 1444.1) * mm, v(6379.23, 1453.6) * mm, v(6378.41, 1466.2) * mm, v(6376.95, 1481.87) * mm, v(6374.52, 1500.47) * mm, v(6371.4, 1518.84) * mm, v(6366.38, 1542.97) * mm, v(6358.48, 1572.38) * mm, v(6348.49, 1600.57) * mm, v(6339.3, 1622.26) * mm, v(6331.8, 1638.06) * mm, v(6323.74, 1653.36) * mm, v(6316.55, 1665.66) * mm, v(6310.52, 1675.23) * mm, v(6305.87, 1682.26) * mm, v(6301.87, 1688) * mm, v(6298.62, 1692.5) * mm, v(6296.14, 1695.85) * mm, v(6293.63, 1699.15) * mm, v(6290.25, 1703.5) * mm, v(6285.97, 1708.8) * mm, v(6280.73, 1714.97) * mm, v(6273.61, 1722.93) * mm, v(6264.5, 1732.4) * mm, v(6253.2, 1742.98) * mm, v(6241.6, 1752.75) * mm, v(6225.75, 1764.7) * mm, v(6205.28, 1777.6) * mm, v(6179.85, 1789.74) * mm, v(6158.09, 1797.03) * mm, v(6140.41, 1801.15) * mm, v(6127.04, 1803.36) * mm, v(6115.81, 1804.48) * mm, v(6106.8, 1804.92) * mm, v(6100, 1805.04) * mm, v(6093.2, 1804.92) * mm, v(6106.8, 1804.92) * mm]});
            skSolve(sketch);
        }
        {
            var Q0;
            Q0 = qSketchRegion(id + "F27", true);
            extrude(context, id + "F28", {"entities" : qUnion([Q0]), "operationType" : NewBodyOperationType.ADD, "depth" : 40 * mm, "offsetDistance" : 25 * mm});
        }
    });
